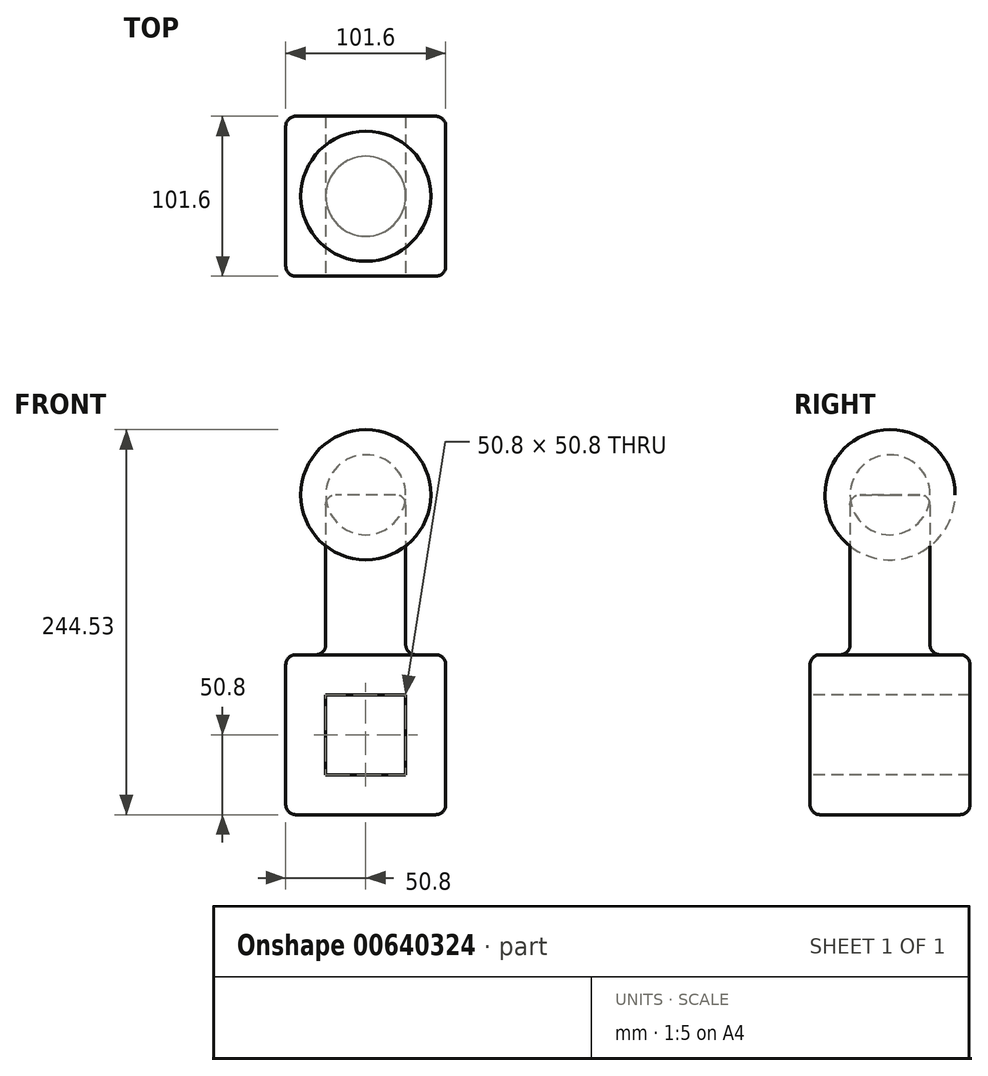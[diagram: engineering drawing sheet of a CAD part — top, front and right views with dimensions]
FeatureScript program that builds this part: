
annotation { "Feature Type Name" : "Feature", "Feature Type Description" : "" }
export const myFeature = defineFeature(function(context is Context, id is Id, definition is map)
    precondition{}
    {
        {
            var Q0;
            Q0=qCreatedBy(makeId("Top.planeOp"),FACE);
            var sketch = newSketch(context, id + "F0", { "sketchPlane" : qUnion([Q0])});
            skSolve(sketch);
        }
        {
            var Q0;
            Q0=qCreatedBy(makeId("Top.planeOp"),FACE);
            var sketch = newSketch(context, id + "F1", { "sketchPlane" : qUnion([Q0])});
            skPoint(sketch, "E0.middle", {"position": v(0, 0) * mm});
            skLineSegment(sketch, "E1.bottom", {"start": v(-50.8, 50.8) * mm, "end": v(50.8, 50.8) * mm});
            skLineSegment(sketch, "E1.top", {"start": v(-50.8, -50.8) * mm, "end": v(50.8, -50.8) * mm});
            skLineSegment(sketch, "E1.left", {"start": v(-50.8, 50.8) * mm, "end": v(-50.8, -50.8) * mm});
            skLineSegment(sketch, "E1.right", {"start": v(50.8, 50.8) * mm, "end": v(50.8, -50.8) * mm});
            skSolve(sketch);
        }
        {
            var Q0;
            Q0=makeQuery(id+"F1.imprint","IMPRINT",FACE,{"disambiguationData":[TD([[makeQuery(id+"F1.imprint","IMPRINT",EDGE,{"derivedFrom":sQuery(id+"F1.wireOp",EDGE,"E1.bottom")}),-1.0]])]});
            extrude(context, id + "F2", {"entities" : qUnion([Q0]), "depth" : 101.6 * mm, "offsetDistance" : 25.4 * mm});
        }
        {
            var Q0;
            Q0=makeQuery(id+"F2.opExtrude","CAP_FACE",FACE,{"disambiguationData":[OSD([sQuery(id+"F1.wireOp",EDGE,"E1.bottom"),sQuery(id+"F1.wireOp",EDGE,"E1.top"),sQuery(id+"F1.wireOp",EDGE,"E1.left"),sQuery(id+"F1.wireOp",EDGE,"E1.right")])],"isStart":false});
            var sketch = newSketch(context, id + "F3", { "sketchPlane" : qUnion([Q0])});
            skCircle(sketch, "E2", {"center": v(0, 0) * mm, "radius": 25.4 * mm});
            skSolve(sketch);
        }
        {
            var Q0;
            Q0=makeQuery(id+"F3.imprint","IMPRINT",FACE,{"disambiguationData":[TD([[makeQuery(id+"F3.imprint","IMPRINT",EDGE,{"derivedFrom":sQuery(id+"F3.wireOp",EDGE,"E2")}),1.0]])]});
            extrude(context, id + "F4", {"entities" : qUnion([Q0]), "operationType" : NewBodyOperationType.ADD, "depth" : 101.6 * mm, "offsetDistance" : 25.4 * mm});
        }
        {
            var Q0;
            Q0=makeQuery(id+"F4.opExtrude","CAP_FACE",FACE,{"disambiguationData":[OSD([sQuery(id+"F3.wireOp",EDGE,"E2")])],"isStart":false});
            var sketch = newSketch(context, id + "F5", { "sketchPlane" : qUnion([Q0])});
            skArc(sketch, "E3", {"start": v(0, -41.33) * mm, "mid": v(41.33, 0) * mm, "end": v(0, 41.33) * mm});
            skLineSegment(sketch, "E4", {"start": v(0, 41.33) * mm, "end": v(0, -41.33) * mm});
            skSolve(sketch);
        }
        {
            var Q0;
            Q0 = qSketchRegion(id + "F0", true);
            var Q1;
            {var subQ0=sQuery(id+"F5.wireOp",EDGE,"E4");var subQ1=makeQuery(id+"F4.opExtrude","CAP_EDGE",EDGE,{"disambiguationData":[OSD([sQuery(id+"F3.wireOp",EDGE,"E2")])],"isStart":false});var subQ2=makeQuery(id+"F5.imprint","INTERSECT",VERTEX,{"disambiguationData":[OD(0.0)],"derivedFrom":[subQ1,subQ0]});Q1=makeQuery(id+"F5.imprint","IMPRINT",FACE,{"disambiguationData":[TD([[makeQuery(id+"F5.imprint","IMPRINT",EDGE,{"disambiguationData":[TD([[subQ2,-1.0]])],"derivedFrom":subQ0}),1.0]])]});}
            var Q2;
            {var subQ0=sQuery(id+"F5.wireOp",EDGE,"E4");var subQ1=makeQuery(id+"F4.opExtrude","CAP_EDGE",EDGE,{"disambiguationData":[OSD([sQuery(id+"F3.wireOp",EDGE,"E2")])],"isStart":false});var subQ2=makeQuery(id+"F5.imprint","INTERSECT",VERTEX,{"disambiguationData":[OD(0.0)],"derivedFrom":[subQ1,subQ0]});Q2=makeQuery(id+"F5.imprint","IMPRINT",FACE,{"disambiguationData":[TD([[makeQuery(id+"F5.imprint","IMPRINT",EDGE,{"disambiguationData":[TD([[subQ2,-1.0]])],"derivedFrom":subQ0}),-1.0]])]});}
            var Q3;
            {var subQ0=sQuery(id+"F5.wireOp",EDGE,"E3");Q3=makeQuery(id+"F5.imprint","IMPRINT",FACE,{"disambiguationData":[TD([[makeQuery(id+"F5.imprint","IMPRINT",EDGE,{"derivedFrom":subQ0}),1.0]])]});}
            var Q4;
            Q4=sQuery(id+"F5.wireOp",EDGE,"E4");
            revolve(context, id + "F6", {"surfaceOperationType" : NewSurfaceOperationType.NEW, "entities" : qUnion([Q0, Q1, Q2, Q3]), "axis" : qUnion([Q4]), "revolveType" : RevolveType.FULL});
        }
        {
            var Q0;
            Q0=makeQuery(id+"F2.opExtrude","SWEPT_FACE",FACE,{"disambiguationData":[OSD([sQuery(id+"F1.wireOp",EDGE,"E1.top")])]});
            var sketch = newSketch(context, id + "F7", { "sketchPlane" : qUnion([Q0])});
            skPoint(sketch, "E5.oppositeSnap0", {"position": v(50.8, 50.8) * mm});
            skLineSegment(sketch, "E5.left", {"start": v(50.8, 50.8) * mm, "end": v(50.8, 50.8) * mm});
            skLineSegment(sketch, "E5.right", {"start": v(0, 50.8) * mm, "end": v(0, 50.8) * mm});
            skLineSegment(sketch, "E6.bottom", {"start": v(25.4, 76.2) * mm, "end": v(-25.4, 76.2) * mm});
            skLineSegment(sketch, "E6.top", {"start": v(25.4, 25.4) * mm, "end": v(-25.4, 25.4) * mm});
            skLineSegment(sketch, "E6.left", {"start": v(25.4, 76.2) * mm, "end": v(25.4, 25.4) * mm});
            skLineSegment(sketch, "E6.right", {"start": v(-25.4, 76.2) * mm, "end": v(-25.4, 25.4) * mm});
            skPoint(sketch, "E6.middle", {"position": v(0, 50.8) * mm});
            skSolve(sketch);
        }
        {
            var Q0;
            Q0=makeQuery(id+"F7.imprint","IMPRINT",FACE,{"disambiguationData":[TD([[makeQuery(id+"F7.imprint","IMPRINT",EDGE,{"derivedFrom":sQuery(id+"F7.wireOp",EDGE,"E6.bottom")}),1.0]])]});
            extrude(context, id + "F8", {"entities" : qUnion([Q0]), "operationType" : NewBodyOperationType.REMOVE, "oppositeDirection" : true, "depth" : 185.17 * mm, "offsetDistance" : 25.4 * mm});
        }
        {
            var Q0;
            Q0=makeQuery(id+"F2.opExtrude","CAP_EDGE",EDGE,{"disambiguationData":[OSD([sQuery(id+"F1.wireOp",EDGE,"E1.right")])],"isStart":false});
            var Q1;
            Q1=makeQuery(id+"F2.opExtrude","CAP_EDGE",EDGE,{"disambiguationData":[OSD([sQuery(id+"F1.wireOp",EDGE,"E1.top")])],"isStart":false});
            var Q2;
            Q2=makeQuery(id+"F2.opExtrude","SWEPT_EDGE",EDGE,{"disambiguationData":[OSD([sQuery(id+"F1.wireOp",EDGE,"E1.top"),sQuery(id+"F1.wireOp",EDGE,"E1.left")])]});
            var Q3;
            Q3=makeQuery(id+"F2.opExtrude","SWEPT_EDGE",EDGE,{"disambiguationData":[OSD([sQuery(id+"F1.wireOp",EDGE,"E1.top"),sQuery(id+"F1.wireOp",EDGE,"E1.right")])]});
            var Q4;
            Q4=makeQuery(id+"F2.opExtrude","SWEPT_EDGE",EDGE,{"disambiguationData":[OSD([sQuery(id+"F1.wireOp",EDGE,"E1.bottom"),sQuery(id+"F1.wireOp",EDGE,"E1.right")])]});
            var Q5;
            Q5=makeQuery(id+"F2.opExtrude","CAP_EDGE",EDGE,{"disambiguationData":[OSD([sQuery(id+"F1.wireOp",EDGE,"E1.right")])],"isStart":true});
            var Q6;
            Q6=makeQuery(id+"F2.opExtrude","CAP_EDGE",EDGE,{"disambiguationData":[OSD([sQuery(id+"F1.wireOp",EDGE,"E1.bottom")])],"isStart":false});
            var Q7;
            Q7=makeQuery(id+"F2.opExtrude","CAP_EDGE",EDGE,{"disambiguationData":[OSD([sQuery(id+"F1.wireOp",EDGE,"E1.left")])],"isStart":false});
            var Q8;
            Q8=makeQuery(id+"F2.opExtrude","CAP_EDGE",EDGE,{"disambiguationData":[OSD([sQuery(id+"F1.wireOp",EDGE,"E1.top")])],"isStart":true});
            var Q9;
            Q9=makeQuery(id+"F2.opExtrude","SWEPT_EDGE",EDGE,{"disambiguationData":[OSD([sQuery(id+"F1.wireOp",EDGE,"E1.bottom"),sQuery(id+"F1.wireOp",EDGE,"E1.left")])]});
            var Q10;
            Q10=makeQuery(id+"F2.opExtrude","CAP_EDGE",EDGE,{"disambiguationData":[OSD([sQuery(id+"F1.wireOp",EDGE,"E1.bottom")])],"isStart":true});
            var Q11;
            Q11=makeQuery(id+"F2.opExtrude","SWEPT_FACE",FACE,{"disambiguationData":[OSD([sQuery(id+"F1.wireOp",EDGE,"E1.left")])]});
            var Q12;
            Q12=makeQuery(id+"F4.opExtrude","CAP_EDGE",EDGE,{"disambiguationData":[OSD([sQuery(id+"F3.wireOp",EDGE,"E2")])],"isStart":true});
            var Q13;
            Q13=makeQuery(id+"F4.opExtrude","SWEPT_FACE",FACE,{"disambiguationData":[OSD([sQuery(id+"F3.wireOp",EDGE,"E2")])]});
            var Q14;
            Q14=makeQuery(id+"F6.opRevolve","SWEPT_FACE",FACE,{"disambiguationData":[OSD([sQuery(id+"F5.wireOp",EDGE,"E3")])]});
            fillet(context, id + "F9", {"entities" : qUnion([Q0, Q1, Q2, Q3, Q4, Q5, Q6, Q7, Q8, Q9, Q10, Q11, Q12, Q13, Q14]), "radius" : 6.35 * mm, "tangentPropagation" : true, "allowEdgeOverflow" : false});
        }
    });
